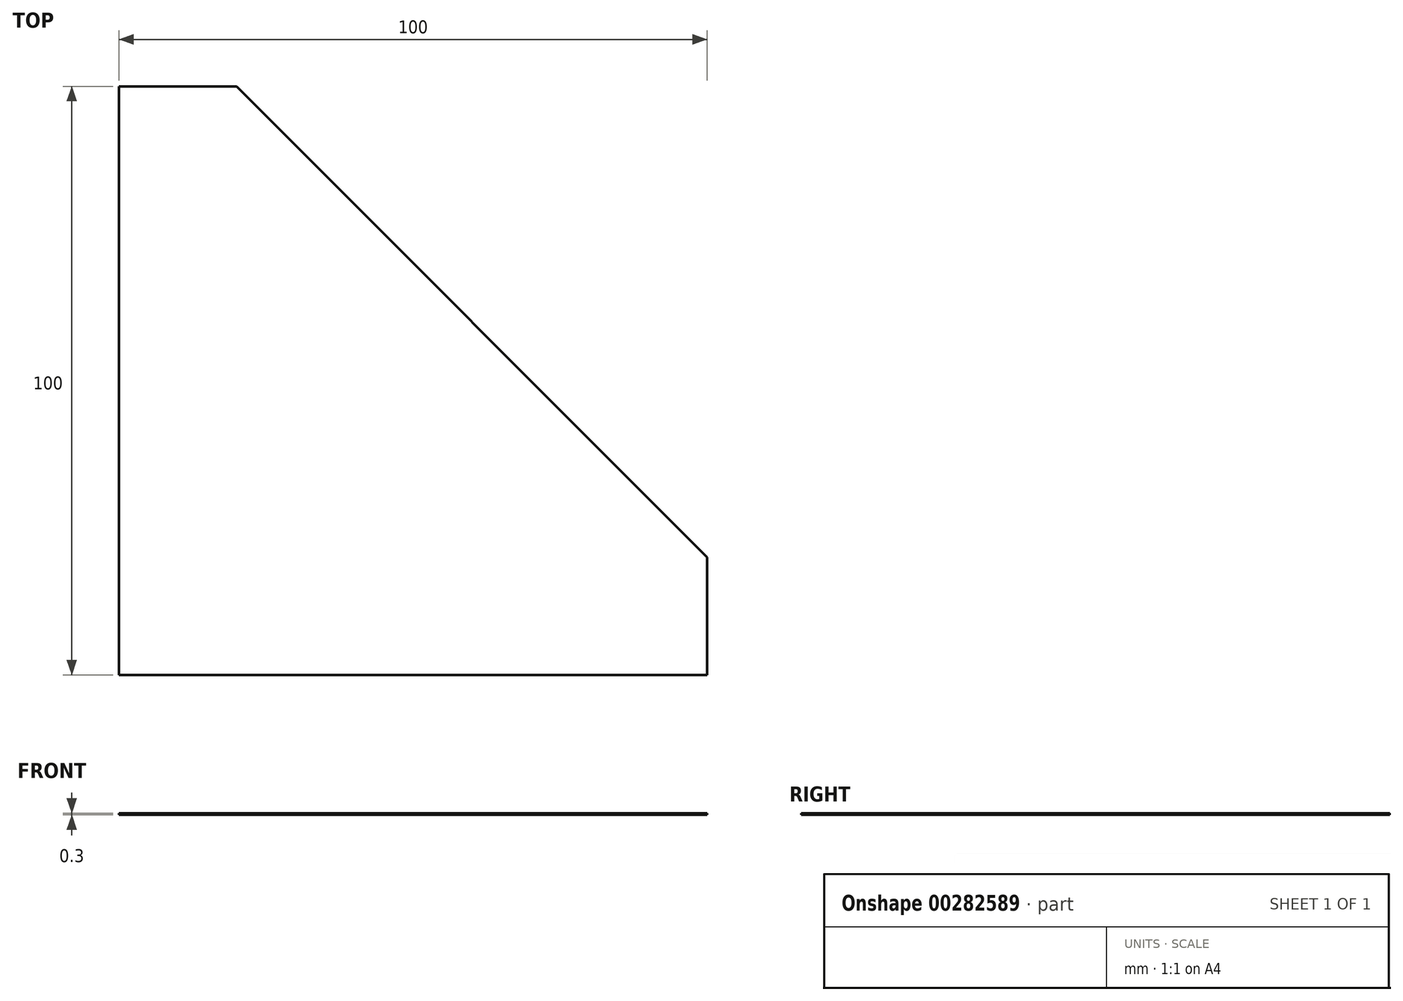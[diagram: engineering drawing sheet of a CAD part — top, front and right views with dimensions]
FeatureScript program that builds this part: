
annotation { "Feature Type Name" : "Feature", "Feature Type Description" : "" }
export const myFeature = defineFeature(function(context is Context, id is Id, definition is map)
    precondition{}
    {
        {
            var Q0;
            Q0=qCreatedBy(makeId("Top.planeOp"),FACE);
            var sketch = newSketch(context, id + "F0", { "sketchPlane" : qUnion([Q0])});
            skLineSegment(sketch, "E0.bottom", {"start": v(50, -50) * mm, "end": v(-50, -50) * mm});
            skLineSegment(sketch, "E0.top", {"start": v(-30, 50) * mm, "end": v(-50, 50) * mm});
            skLineSegment(sketch, "E0.left", {"start": v(50, -50) * mm, "end": v(50, -30) * mm});
            skLineSegment(sketch, "E0.right", {"start": v(-50, -50) * mm, "end": v(-50, 50) * mm});
            skPoint(sketch, "E0.middle", {"position": v(0, 0) * mm});
            skLineSegment(sketch, "E1", {"start": v(-30, 50) * mm, "end": v(50, -30) * mm});
            skSolve(sketch);
        }
        {
            var Q0;
            Q0=makeQuery(id+"F0.imprint","IMPRINT",FACE,{"disambiguationData":[TD([[makeQuery(id+"F0.imprint","IMPRINT",EDGE,{"derivedFrom":sQuery(id+"F0.wireOp",EDGE,"E0.bottom")}),-1.0]])]});
            extrude(context, id + "F1", {"entities" : qUnion([Q0]), "depth" : 0.3 * mm});
        }
    });
